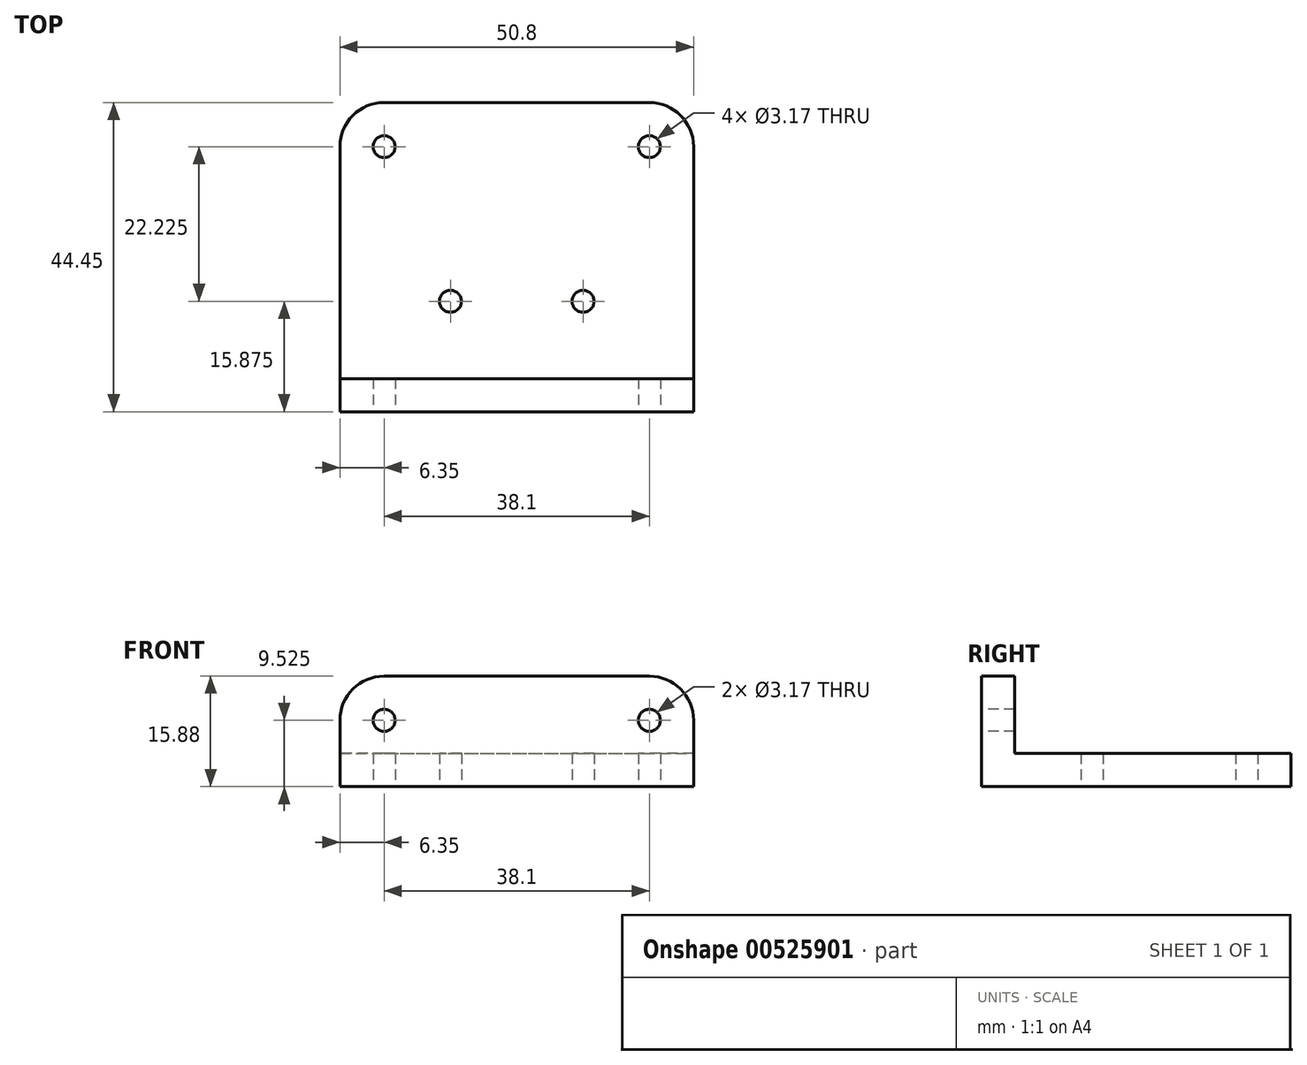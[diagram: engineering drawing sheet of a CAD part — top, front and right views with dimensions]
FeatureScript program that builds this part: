
annotation { "Feature Type Name" : "Feature", "Feature Type Description" : "" }
export const myFeature = defineFeature(function(context is Context, id is Id, definition is map)
    precondition{}
    {
        {
            var Q0;
            Q0=qCreatedBy(makeId("Top.planeOp"),FACE);
            var sketch = newSketch(context, id + "F0", { "sketchPlane" : qUnion([Q0])});
            skLineSegment(sketch, "E0.bottom", {"start": v(0, 0) * mm, "end": v(50.8, 0) * mm});
            skLineSegment(sketch, "E0.top", {"start": v(6.35, 44.45) * mm, "end": v(44.45, 44.45) * mm});
            skLineSegment(sketch, "E0.left", {"start": v(0, 0) * mm, "end": v(0, 38.1) * mm});
            skLineSegment(sketch, "E0.right", {"start": v(50.8, 0) * mm, "end": v(50.8, 38.1) * mm});
            skCircle(sketch, "E1", {"center": v(6.35, 38.1) * mm, "radius": 1.59 * mm});
            skPoint(sketch, "E2.visualSharp", {"position": v(0, 44.45) * mm});
            skArc(sketch, "E2.filletArc", {"start": v(6.35, 44.45) * mm, "mid": v(1.86, 42.6) * mm, "end": v(0, 38.1) * mm});
            skCircle(sketch, "E3", {"center": v(44.45, 38.1) * mm, "radius": 1.59 * mm});
            skPoint(sketch, "E4.visualSharp", {"position": v(50.8, 44.45) * mm});
            skArc(sketch, "E4.filletArc", {"start": v(50.8, 38.1) * mm, "mid": v(48.94, 42.6) * mm, "end": v(44.45, 44.45) * mm});
            skLineSegment(sketch, "E5", {"start": v(0, 4.76) * mm, "end": v(50.8, 4.76) * mm});
            skCircle(sketch, "E6", {"center": v(15.87, 15.88) * mm, "radius": 1.59 * mm});
            skLineSegment(sketch, "E7.MirrorCS", {"start": v(0, 84.14) * mm, "end": v(50.8, 84.14) * mm});
            skCircle(sketch, "E8", {"center": v(34.93, 15.88) * mm, "radius": 1.59 * mm});
            skSolve(sketch);
        }
        {
            var Q0;
            {var subQ0=sQuery(id+"F0.wireOp",EDGE,"E0.bottom");Q0=makeQuery(id+"F0.imprint","IMPRINT",FACE,{"disambiguationData":[TD([[makeQuery(id+"F0.imprint","IMPRINT",EDGE,{"derivedFrom":subQ0}),1.0]])]});}
            extrude(context, id + "F1", {"entities" : qUnion([Q0]), "depth" : 15.88 * mm, "offsetDistance" : 25.4 * mm});
        }
        {
            var Q0;
            Q0 = qSketchRegion(id + "F0", true);
            extrude(context, id + "F2", {"entities" : qUnion([Q0]), "operationType" : NewBodyOperationType.ADD, "depth" : 4.76 * mm, "offsetDistance" : 25.4 * mm});
        }
        {
            var Q0;
            Q0=makeQuery(id+"F1.opExtrude","SWEPT_FACE",FACE,{"disambiguationData":[OSD([sQuery(id+"F0.wireOp",EDGE,"E0.bottom")])]});
            var sketch = newSketch(context, id + "F3", { "sketchPlane" : qUnion([Q0])});
            skCircle(sketch, "E9", {"center": v(6.35, 9.52) * mm, "radius": 1.59 * mm});
            skLineSegment(sketch, "E10.bottom", {"start": v(6.35, 15.88) * mm, "end": v(6.35, 15.88) * mm});
            skLineSegment(sketch, "E10.top", {"start": v(0, 9.52) * mm, "end": v(6.35, 9.52) * mm});
            skLineSegment(sketch, "E10.left", {"start": v(0, 9.53) * mm, "end": v(0, 9.52) * mm});
            skLineSegment(sketch, "E10.right", {"start": v(6.35, 15.88) * mm, "end": v(6.35, 9.52) * mm});
            skPoint(sketch, "E11.visualSharp", {"position": v(0, 15.88) * mm});
            skArc(sketch, "E11.filletArc", {"start": v(6.35, 15.88) * mm, "mid": v(1.86, 14.02) * mm, "end": v(0, 9.52) * mm});
            skCircle(sketch, "E12", {"center": v(44.45, 9.52) * mm, "radius": 1.59 * mm});
            skLineSegment(sketch, "E13.bottom", {"start": v(44.45, 15.88) * mm, "end": v(44.45, 15.88) * mm});
            skLineSegment(sketch, "E13.top", {"start": v(50.8, 9.52) * mm, "end": v(44.45, 9.52) * mm});
            skLineSegment(sketch, "E13.left", {"start": v(50.8, 9.53) * mm, "end": v(50.8, 9.52) * mm});
            skLineSegment(sketch, "E13.right", {"start": v(44.45, 15.88) * mm, "end": v(44.45, 9.52) * mm});
            skPoint(sketch, "E14.visualSharp", {"position": v(50.8, 15.88) * mm});
            skArc(sketch, "E14.filletArc", {"start": v(50.8, 9.53) * mm, "mid": v(48.94, 14.02) * mm, "end": v(44.45, 15.88) * mm});
            skSolve(sketch);
        }
        {
            var Q0;
            {var subQ0=sQuery(id+"F3.wireOp",EDGE,"E11.filletArc");Q0=makeQuery(id+"F3.imprint","IMPRINT",FACE,{"disambiguationData":[TD([[makeQuery(id+"F3.imprint","IMPRINT",EDGE,{"derivedFrom":subQ0}),-1.0]])]});}
            var Q1;
            {var subQ0=sQuery(id+"F3.wireOp",EDGE,"E10.top");var subQ1=sQuery(id+"F3.wireOp",EDGE,"E9");var subQ2=makeQuery(id+"F3.imprint","INTERSECT",VERTEX,{"derivedFrom":[subQ1,subQ0]});Q1=makeQuery(id+"F3.imprint","IMPRINT",FACE,{"disambiguationData":[TD([[makeQuery(id+"F3.imprint","IMPRINT",EDGE,{"disambiguationData":[TD([[subQ2,1.0]])],"derivedFrom":subQ1}),1.0]])]});}
            var Q2;
            {var subQ0=sQuery(id+"F3.wireOp",EDGE,"E10.top");var subQ1=sQuery(id+"F3.wireOp",EDGE,"E9");var subQ2=makeQuery(id+"F3.imprint","INTERSECT",VERTEX,{"derivedFrom":[subQ1,subQ0]});Q2=makeQuery(id+"F3.imprint","IMPRINT",FACE,{"disambiguationData":[TD([[makeQuery(id+"F3.imprint","IMPRINT",EDGE,{"disambiguationData":[TD([[subQ2,-1.0]])],"derivedFrom":subQ1}),1.0]])]});}
            var Q3;
            {var subQ0=sQuery(id+"F3.wireOp",EDGE,"E14.filletArc");Q3=makeQuery(id+"F3.imprint","IMPRINT",FACE,{"disambiguationData":[TD([[makeQuery(id+"F3.imprint","IMPRINT",EDGE,{"derivedFrom":subQ0}),-1.0]])]});}
            var Q4;
            {var subQ0=sQuery(id+"F3.wireOp",EDGE,"E13.top");var subQ1=sQuery(id+"F3.wireOp",EDGE,"E12");var subQ2=makeQuery(id+"F3.imprint","INTERSECT",VERTEX,{"derivedFrom":[subQ1,subQ0]});Q4=makeQuery(id+"F3.imprint","IMPRINT",FACE,{"disambiguationData":[TD([[makeQuery(id+"F3.imprint","IMPRINT",EDGE,{"disambiguationData":[TD([[subQ2,1.0]])],"derivedFrom":subQ1}),1.0]])]});}
            var Q5;
            {var subQ0=sQuery(id+"F3.wireOp",EDGE,"E13.top");var subQ1=sQuery(id+"F3.wireOp",EDGE,"E12");var subQ2=makeQuery(id+"F3.imprint","INTERSECT",VERTEX,{"derivedFrom":[subQ1,subQ0]});Q5=makeQuery(id+"F3.imprint","IMPRINT",FACE,{"disambiguationData":[TD([[makeQuery(id+"F3.imprint","IMPRINT",EDGE,{"disambiguationData":[TD([[subQ2,-1.0]])],"derivedFrom":subQ1}),1.0]])]});}
            extrude(context, id + "F4", {"entities" : qUnion([Q0, Q1, Q2, Q3, Q4, Q5]), "operationType" : NewBodyOperationType.REMOVE, "oppositeDirection" : true, "depth" : 25.4 * mm, "offsetDistance" : 25.4 * mm});
        }
    });
